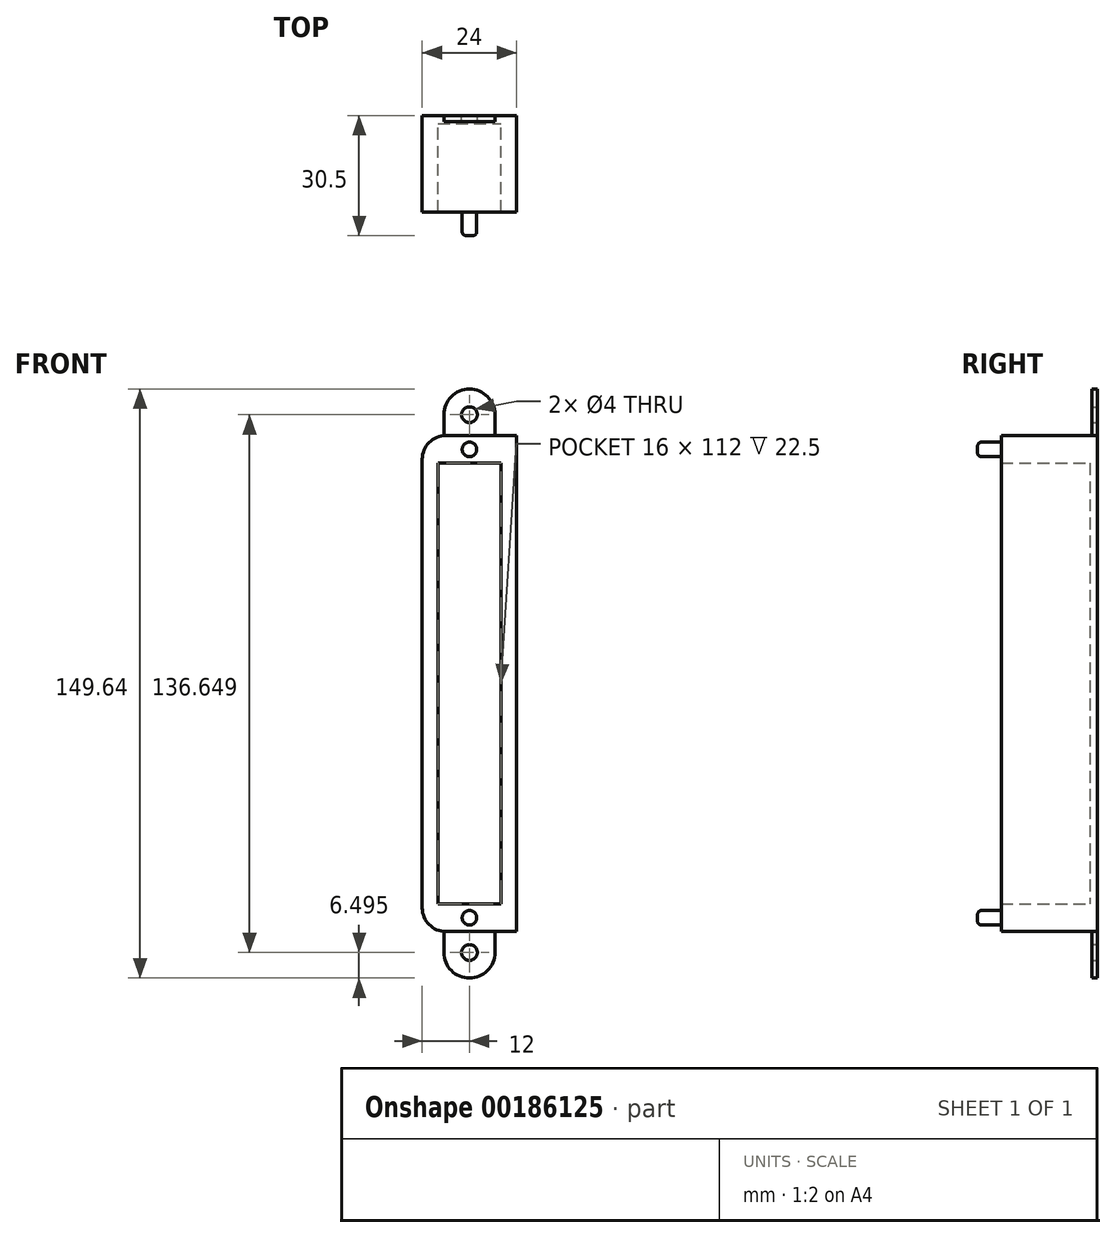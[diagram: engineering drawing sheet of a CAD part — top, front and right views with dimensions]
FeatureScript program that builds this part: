
annotation { "Feature Type Name" : "Feature", "Feature Type Description" : "" }
export const myFeature = defineFeature(function(context is Context, id is Id, definition is map)
    precondition{}
    {
        {
            var Q0;
            Q0=qCreatedBy(makeId("Front.planeOp"),FACE);
            var sketch = newSketch(context, id + "F0", { "sketchPlane" : qUnion([Q0])});
            skLineSegment(sketch, "E0.bottom", {"start": v(-12, 63) * mm, "end": v(12, 63) * mm});
            skLineSegment(sketch, "E0.top", {"start": v(-12, -63) * mm, "end": v(12, -63) * mm});
            skLineSegment(sketch, "E0.left", {"start": v(-12, 63) * mm, "end": v(-12, -63) * mm});
            skLineSegment(sketch, "E0.right", {"start": v(12, 63) * mm, "end": v(12, -63) * mm});
            skPoint(sketch, "E1", {"position": v(0, 63) * mm});
            skPoint(sketch, "E2", {"position": v(-12, 0) * mm});
            skLineSegment(sketch, "E3.bottom", {"start": v(-8, 56) * mm, "end": v(8, 56) * mm});
            skLineSegment(sketch, "E3.top", {"start": v(-8, -56) * mm, "end": v(8, -56) * mm});
            skLineSegment(sketch, "E3.left", {"start": v(-8, 56) * mm, "end": v(-8, -56) * mm});
            skLineSegment(sketch, "E3.right", {"start": v(8, 56) * mm, "end": v(8, -56) * mm});
            skPoint(sketch, "E4", {"position": v(0, 56) * mm});
            skPoint(sketch, "E5", {"position": v(8, 0) * mm});
            skSolve(sketch);
        }
        {
            var Q0;
            Q0 = qSketchRegion(id + "F0", true);
            extrude(context, id + "F1", {"entities" : qUnion([Q0]), "depth" : 24.5 * mm});
        }
        {
            var Q0;
            Q0=makeQuery(id+"F0.imprint","IMPRINT",FACE,{"disambiguationData":[TD([[makeQuery(id+"F0.imprint","IMPRINT",EDGE,{"derivedFrom":sQuery(id+"F0.wireOp",EDGE,"E3.bottom")}),-1.0]])]});
            extrude(context, id + "F2", {"entities" : qUnion([Q0]), "operationType" : NewBodyOperationType.ADD, "depth" : 2 * mm});
        }
        {
            var Q0;
            Q0=makeQuery(id+"F1.opExtrude","CAP_FACE",FACE,{"disambiguationData":[OSD([sQuery(id+"F0.wireOp",EDGE,"E0.bottom"),sQuery(id+"F0.wireOp",EDGE,"E0.top"),sQuery(id+"F0.wireOp",EDGE,"E0.left"),sQuery(id+"F0.wireOp",EDGE,"E0.right"),sQuery(id+"F0.wireOp",EDGE,"E3.bottom"),sQuery(id+"F0.wireOp",EDGE,"E3.top"),sQuery(id+"F0.wireOp",EDGE,"E3.left"),sQuery(id+"F0.wireOp",EDGE,"E3.right")])],"isStart":false});
            var sketch = newSketch(context, id + "F3", { "sketchPlane" : qUnion([Q0])});
            skCircle(sketch, "E6", {"center": v(0, 59.5) * mm, "radius": 1.85 * mm});
            skCircle(sketch, "E7.MirrorC", {"center": v(0, -59.5) * mm, "radius": 1.85 * mm});
            skLineSegment(sketch, "E8", {"start": v(0, 63) * mm, "end": v(0, 56) * mm});
            skSolve(sketch);
        }
        {
            var Q0;
            Q0 = qSketchRegion(id + "F3", true);
            extrude(context, id + "F4", {"entities" : qUnion([Q0]), "operationType" : NewBodyOperationType.ADD, "depth" : 6 * mm});
        }
        {
            var Q0;
            Q0=makeQuery(id+"F1.opExtrude","SWEPT_EDGE",EDGE,{"disambiguationData":[OSD([sQuery(id+"F0.wireOp",EDGE,"E0.top"),sQuery(id+"F0.wireOp",EDGE,"E0.left")])]});
            var Q1;
            Q1=makeQuery(id+"F1.opExtrude","SWEPT_EDGE",EDGE,{"disambiguationData":[OSD([sQuery(id+"F0.wireOp",EDGE,"E0.bottom"),sQuery(id+"F0.wireOp",EDGE,"E0.left")])]});
            fillet(context, id + "F5", {"entities" : qUnion([Q0, Q1]), "radius" : 6 * mm, "tangentPropagation" : true, "allowEdgeOverflow" : false});
        }
        {
            var Q0;
            Q0=qCreatedBy(makeId("Front.planeOp"),FACE);
            var sketch = newSketch(context, id + "F6", { "sketchPlane" : qUnion([Q0])});
            skCircle(sketch, "E9", {"center": v(0, 68.32) * mm, "radius": 2 * mm});
            skLineSegment(sketch, "E10", {"start": v(6.5, 68.32) * mm, "end": v(6.5, 63) * mm});
            skArc(sketch, "E11", {"start": v(6.5, 68.32) * mm, "mid": v(0, 74.82) * mm, "end": v(-6.5, 68.32) * mm});
            skLineSegment(sketch, "E12", {"start": v(-6.5, 63) * mm, "end": v(6.5, 63) * mm});
            skLineSegment(sketch, "E13", {"start": v(12, 63) * mm, "end": v(-12, 63) * mm});
            skLineSegment(sketch, "E14", {"start": v(-6.5, 68.32) * mm, "end": v(-6.5, 62.98) * mm});
            skArc(sketch, "E15.MirrorCS", {"start": v(6.5, -68.32) * mm, "mid": v(0, -74.82) * mm, "end": v(-6.5, -68.32) * mm});
            skCircle(sketch, "E16.MirrorC", {"center": v(0, -68.32) * mm, "radius": 2 * mm});
            skLineSegment(sketch, "E17.MirrorCS", {"start": v(6.5, -68.32) * mm, "end": v(6.5, -63) * mm});
            skLineSegment(sketch, "E18.MirrorCS", {"start": v(-6.5, -68.32) * mm, "end": v(-6.5, -62.98) * mm});
            skArc(sketch, "E19", {"start": v(-6, 63) * mm, "mid": v(-6.25, 63) * mm, "end": v(-6.5, 62.98) * mm});
            skLineSegment(sketch, "E20", {"start": v(-6, 63) * mm, "end": v(6.5, 63) * mm});
            skArc(sketch, "E21.MirrorCS", {"start": v(-6, -63) * mm, "mid": v(-6.25, -63) * mm, "end": v(-6.5, -62.98) * mm});
            skLineSegment(sketch, "E22.MirrorCS", {"start": v(-6, -63) * mm, "end": v(6.5, -63) * mm});
            skSolve(sketch);
        }
        {
            var Q0;
            Q0 = qSketchRegion(id + "F6", true);
            extrude(context, id + "F7", {"entities" : qUnion([Q0]), "operationType" : NewBodyOperationType.ADD, "depth" : 1.5 * mm});
        }
        {
            var Q0;
            Q0=makeQuery(id+"F4.opExtrude","CAP_FACE",FACE,{"disambiguationData":[OSD([sQuery(id+"F3.wireOp",EDGE,"E6")])],"isStart":false});
            var Q1;
            Q1=makeQuery(id+"F4.opExtrude","CAP_EDGE",EDGE,{"disambiguationData":[OSD([sQuery(id+"F3.wireOp",EDGE,"E7.MirrorC")])],"isStart":false});
            fillet(context, id + "F8", {"entities" : qUnion([Q0, Q1]), "radius" : 1 * mm, "tangentPropagation" : true, "allowEdgeOverflow" : false});
        }
    });
